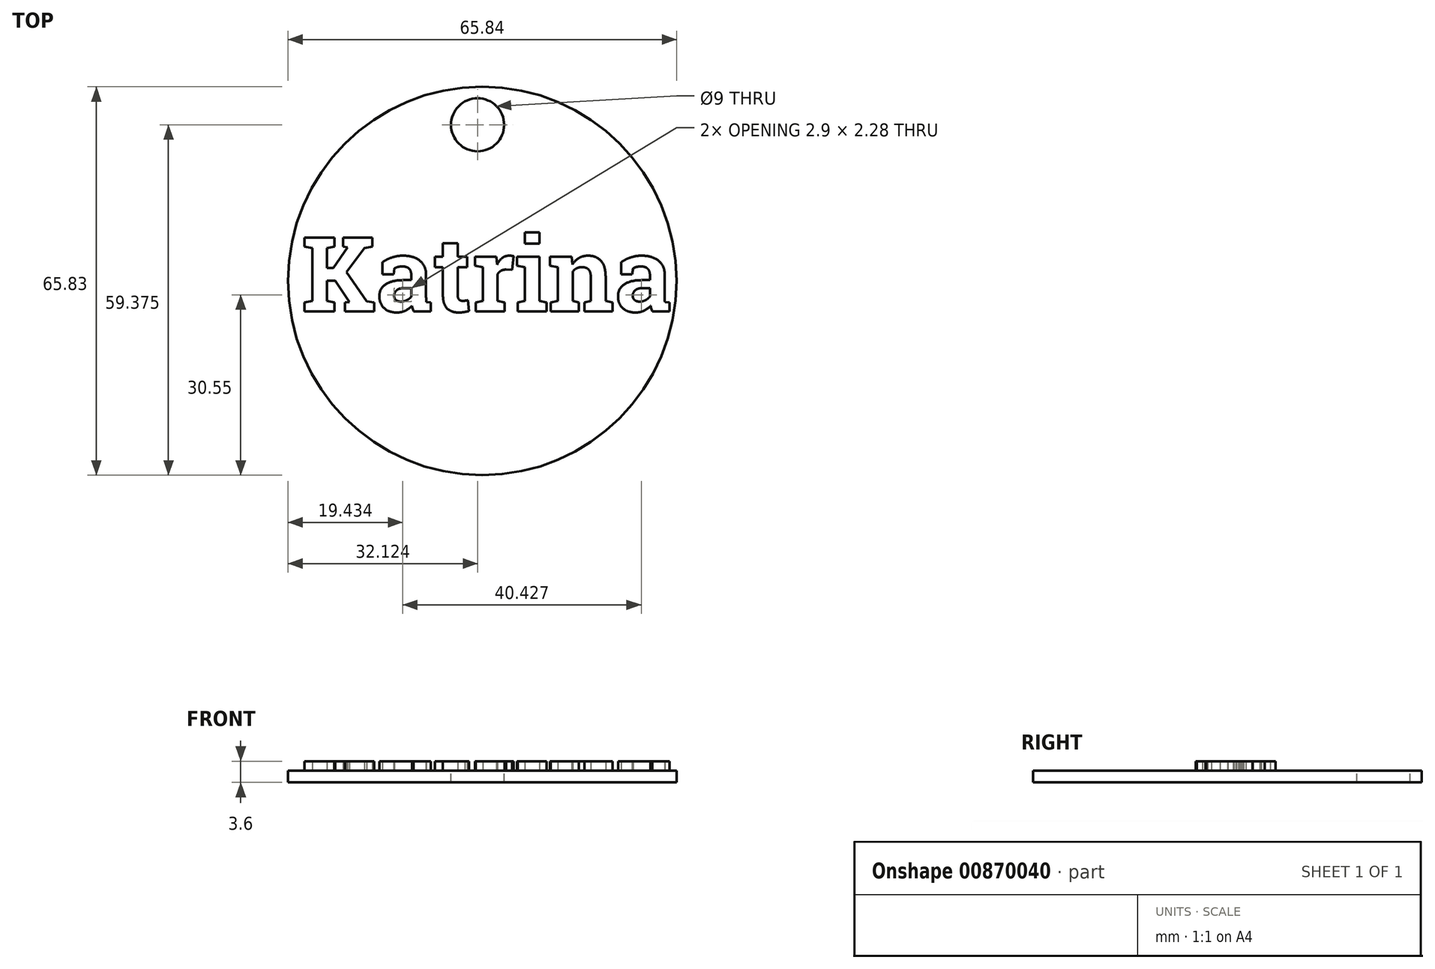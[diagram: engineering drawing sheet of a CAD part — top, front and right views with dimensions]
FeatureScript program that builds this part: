
annotation { "Feature Type Name" : "Feature", "Feature Type Description" : "" }
export const myFeature = defineFeature(function(context is Context, id is Id, definition is map)
    precondition{}
    {
        {
            var Q0;
            Q0=qCreatedBy(makeId("Top.planeOp"),FACE);
            var sketch = newSketch(context, id + "F0", { "sketchPlane" : qUnion([Q0])});
            skText(sketch, "E0", { "text": "Katrina", "fontName": "RobotoSlab-Bold.ttf"});
            const initialGuessF0  = {"E0": [-0.08255, 0.0103, 1, 0, 0.03163]};
            skSetInitialGuess(sketch, initialGuessF0);
            skSolve(sketch);
        }
        {
            var Q0;
            Q0 = qSketchRegion(id + "F0", true);
            extrude(context, id + "F1", {"entities" : qUnion([Q0]), "depth" : 4 * mm, "offsetDistance" : 25.4 * mm});
        }
        {
            var Q0;
            Q0=makeQuery(id+"F1.opExtrude","SWEPT_BODY",BODY,{"disambiguationData":[OSD([sQuery(id+"F0.wireOp",EDGE,"E0.sketch_text.stroke-143"),sQuery(id+"F0.wireOp",EDGE,"E0.sketch_text.stroke-144"),sQuery(id+"F0.wireOp",EDGE,"E0.sketch_text.stroke-145"),sQuery(id+"F0.wireOp",EDGE,"E0.sketch_text.stroke-146"),sQuery(id+"F0.wireOp",EDGE,"E0.sketch_text.stroke-147"),sQuery(id+"F0.wireOp",EDGE,"E0.sketch_text.stroke-148"),sQuery(id+"F0.wireOp",EDGE,"E0.sketch_text.stroke-149"),sQuery(id+"F0.wireOp",EDGE,"E0.sketch_text.stroke-150"),sQuery(id+"F0.wireOp",EDGE,"E0.sketch_text.stroke-151"),sQuery(id+"F0.wireOp",EDGE,"E0.sketch_text.stroke-152"),sQuery(id+"F0.wireOp",EDGE,"E0.sketch_text.stroke-153"),sQuery(id+"F0.wireOp",EDGE,"E0.sketch_text.stroke-154"),sQuery(id+"F0.wireOp",EDGE,"E0.sketch_text.stroke-155"),sQuery(id+"F0.wireOp",EDGE,"E0.sketch_text.stroke-156"),sQuery(id+"F0.wireOp",EDGE,"E0.sketch_text.stroke-157"),sQuery(id+"F0.wireOp",EDGE,"E0.sketch_text.stroke-158"),sQuery(id+"F0.wireOp",EDGE,"E0.sketch_text.stroke-159"),sQuery(id+"F0.wireOp",EDGE,"E0.sketch_text.stroke-160"),sQuery(id+"F0.wireOp",EDGE,"E0.sketch_text.stroke-161"),sQuery(id+"F0.wireOp",EDGE,"E0.sketch_text.stroke-162"),sQuery(id+"F0.wireOp",EDGE,"E0.sketch_text.stroke-163"),sQuery(id+"F0.wireOp",EDGE,"E0.sketch_text.stroke-164"),sQuery(id+"F0.wireOp",EDGE,"E0.sketch_text.stroke-165"),sQuery(id+"F0.wireOp",EDGE,"E0.sketch_text.stroke-166"),sQuery(id+"F0.wireOp",EDGE,"E0.sketch_text.stroke-167"),sQuery(id+"F0.wireOp",EDGE,"E0.sketch_text.stroke-168"),sQuery(id+"F0.wireOp",EDGE,"E0.sketch_text.stroke-169"),sQuery(id+"F0.wireOp",EDGE,"E0.sketch_text.stroke-170"),sQuery(id+"F0.wireOp",EDGE,"E0.sketch_text.stroke-171"),sQuery(id+"F0.wireOp",EDGE,"E0.sketch_text.stroke-172"),sQuery(id+"F0.wireOp",EDGE,"E0.sketch_text.stroke-173"),sQuery(id+"F0.wireOp",EDGE,"E0.sketch_text.stroke-174"),sQuery(id+"F0.wireOp",EDGE,"E0.sketch_text.stroke-175"),sQuery(id+"F0.wireOp",EDGE,"E0.sketch_text.stroke-176"),sQuery(id+"F0.wireOp",EDGE,"E0.sketch_text.stroke-177")])]});
            var Q1;
            Q1=makeQuery(id+"F1.opExtrude","SWEPT_BODY",BODY,{"disambiguationData":[OSD([sQuery(id+"F0.wireOp",EDGE,"E0.sketch_text.stroke-0"),sQuery(id+"F0.wireOp",EDGE,"E0.sketch_text.stroke-1"),sQuery(id+"F0.wireOp",EDGE,"E0.sketch_text.stroke-2"),sQuery(id+"F0.wireOp",EDGE,"E0.sketch_text.stroke-3"),sQuery(id+"F0.wireOp",EDGE,"E0.sketch_text.stroke-4"),sQuery(id+"F0.wireOp",EDGE,"E0.sketch_text.stroke-5"),sQuery(id+"F0.wireOp",EDGE,"E0.sketch_text.stroke-6"),sQuery(id+"F0.wireOp",EDGE,"E0.sketch_text.stroke-7"),sQuery(id+"F0.wireOp",EDGE,"E0.sketch_text.stroke-8"),sQuery(id+"F0.wireOp",EDGE,"E0.sketch_text.stroke-9"),sQuery(id+"F0.wireOp",EDGE,"E0.sketch_text.stroke-10"),sQuery(id+"F0.wireOp",EDGE,"E0.sketch_text.stroke-11"),sQuery(id+"F0.wireOp",EDGE,"E0.sketch_text.stroke-12"),sQuery(id+"F0.wireOp",EDGE,"E0.sketch_text.stroke-13"),sQuery(id+"F0.wireOp",EDGE,"E0.sketch_text.stroke-14"),sQuery(id+"F0.wireOp",EDGE,"E0.sketch_text.stroke-15"),sQuery(id+"F0.wireOp",EDGE,"E0.sketch_text.stroke-16"),sQuery(id+"F0.wireOp",EDGE,"E0.sketch_text.stroke-17"),sQuery(id+"F0.wireOp",EDGE,"E0.sketch_text.stroke-18"),sQuery(id+"F0.wireOp",EDGE,"E0.sketch_text.stroke-19"),sQuery(id+"F0.wireOp",EDGE,"E0.sketch_text.stroke-20"),sQuery(id+"F0.wireOp",EDGE,"E0.sketch_text.stroke-21"),sQuery(id+"F0.wireOp",EDGE,"E0.sketch_text.stroke-22"),sQuery(id+"F0.wireOp",EDGE,"E0.sketch_text.stroke-23"),sQuery(id+"F0.wireOp",EDGE,"E0.sketch_text.stroke-24"),sQuery(id+"F0.wireOp",EDGE,"E0.sketch_text.stroke-25"),sQuery(id+"F0.wireOp",EDGE,"E0.sketch_text.stroke-26"),sQuery(id+"F0.wireOp",EDGE,"E0.sketch_text.stroke-27"),sQuery(id+"F0.wireOp",EDGE,"E0.sketch_text.stroke-28")])]});
            var Q2;
            Q2=makeQuery(id+"F1.opExtrude","SWEPT_BODY",BODY,{"disambiguationData":[OSD([sQuery(id+"F0.wireOp",EDGE,"E0.sketch_text.stroke-29"),sQuery(id+"F0.wireOp",EDGE,"E0.sketch_text.stroke-30"),sQuery(id+"F0.wireOp",EDGE,"E0.sketch_text.stroke-31"),sQuery(id+"F0.wireOp",EDGE,"E0.sketch_text.stroke-32"),sQuery(id+"F0.wireOp",EDGE,"E0.sketch_text.stroke-33"),sQuery(id+"F0.wireOp",EDGE,"E0.sketch_text.stroke-34"),sQuery(id+"F0.wireOp",EDGE,"E0.sketch_text.stroke-35"),sQuery(id+"F0.wireOp",EDGE,"E0.sketch_text.stroke-36"),sQuery(id+"F0.wireOp",EDGE,"E0.sketch_text.stroke-37"),sQuery(id+"F0.wireOp",EDGE,"E0.sketch_text.stroke-38"),sQuery(id+"F0.wireOp",EDGE,"E0.sketch_text.stroke-39"),sQuery(id+"F0.wireOp",EDGE,"E0.sketch_text.stroke-40"),sQuery(id+"F0.wireOp",EDGE,"E0.sketch_text.stroke-41"),sQuery(id+"F0.wireOp",EDGE,"E0.sketch_text.stroke-42"),sQuery(id+"F0.wireOp",EDGE,"E0.sketch_text.stroke-43"),sQuery(id+"F0.wireOp",EDGE,"E0.sketch_text.stroke-44"),sQuery(id+"F0.wireOp",EDGE,"E0.sketch_text.stroke-45"),sQuery(id+"F0.wireOp",EDGE,"E0.sketch_text.stroke-46"),sQuery(id+"F0.wireOp",EDGE,"E0.sketch_text.stroke-47"),sQuery(id+"F0.wireOp",EDGE,"E0.sketch_text.stroke-48"),sQuery(id+"F0.wireOp",EDGE,"E0.sketch_text.stroke-49"),sQuery(id+"F0.wireOp",EDGE,"E0.sketch_text.stroke-50"),sQuery(id+"F0.wireOp",EDGE,"E0.sketch_text.stroke-51"),sQuery(id+"F0.wireOp",EDGE,"E0.sketch_text.stroke-52"),sQuery(id+"F0.wireOp",EDGE,"E0.sketch_text.stroke-53"),sQuery(id+"F0.wireOp",EDGE,"E0.sketch_text.stroke-54"),sQuery(id+"F0.wireOp",EDGE,"E0.sketch_text.stroke-55"),sQuery(id+"F0.wireOp",EDGE,"E0.sketch_text.stroke-56"),sQuery(id+"F0.wireOp",EDGE,"E0.sketch_text.stroke-57"),sQuery(id+"F0.wireOp",EDGE,"E0.sketch_text.stroke-58"),sQuery(id+"F0.wireOp",EDGE,"E0.sketch_text.stroke-59"),sQuery(id+"F0.wireOp",EDGE,"E0.sketch_text.stroke-60"),sQuery(id+"F0.wireOp",EDGE,"E0.sketch_text.stroke-61"),sQuery(id+"F0.wireOp",EDGE,"E0.sketch_text.stroke-62"),sQuery(id+"F0.wireOp",EDGE,"E0.sketch_text.stroke-63")])]});
            var Q3;
            Q3=makeQuery(id+"F1.opExtrude","SWEPT_BODY",BODY,{"disambiguationData":[OSD([sQuery(id+"F0.wireOp",EDGE,"E0.sketch_text.stroke-64"),sQuery(id+"F0.wireOp",EDGE,"E0.sketch_text.stroke-65"),sQuery(id+"F0.wireOp",EDGE,"E0.sketch_text.stroke-66"),sQuery(id+"F0.wireOp",EDGE,"E0.sketch_text.stroke-67"),sQuery(id+"F0.wireOp",EDGE,"E0.sketch_text.stroke-68"),sQuery(id+"F0.wireOp",EDGE,"E0.sketch_text.stroke-69"),sQuery(id+"F0.wireOp",EDGE,"E0.sketch_text.stroke-70"),sQuery(id+"F0.wireOp",EDGE,"E0.sketch_text.stroke-71"),sQuery(id+"F0.wireOp",EDGE,"E0.sketch_text.stroke-72"),sQuery(id+"F0.wireOp",EDGE,"E0.sketch_text.stroke-73"),sQuery(id+"F0.wireOp",EDGE,"E0.sketch_text.stroke-74"),sQuery(id+"F0.wireOp",EDGE,"E0.sketch_text.stroke-75"),sQuery(id+"F0.wireOp",EDGE,"E0.sketch_text.stroke-76"),sQuery(id+"F0.wireOp",EDGE,"E0.sketch_text.stroke-77"),sQuery(id+"F0.wireOp",EDGE,"E0.sketch_text.stroke-78"),sQuery(id+"F0.wireOp",EDGE,"E0.sketch_text.stroke-79"),sQuery(id+"F0.wireOp",EDGE,"E0.sketch_text.stroke-80"),sQuery(id+"F0.wireOp",EDGE,"E0.sketch_text.stroke-81"),sQuery(id+"F0.wireOp",EDGE,"E0.sketch_text.stroke-82"),sQuery(id+"F0.wireOp",EDGE,"E0.sketch_text.stroke-83")])]});
            var Q4;
            Q4=makeQuery(id+"F1.opExtrude","SWEPT_BODY",BODY,{"disambiguationData":[OSD([sQuery(id+"F0.wireOp",EDGE,"E0.sketch_text.stroke-84"),sQuery(id+"F0.wireOp",EDGE,"E0.sketch_text.stroke-85"),sQuery(id+"F0.wireOp",EDGE,"E0.sketch_text.stroke-86"),sQuery(id+"F0.wireOp",EDGE,"E0.sketch_text.stroke-87"),sQuery(id+"F0.wireOp",EDGE,"E0.sketch_text.stroke-88"),sQuery(id+"F0.wireOp",EDGE,"E0.sketch_text.stroke-89"),sQuery(id+"F0.wireOp",EDGE,"E0.sketch_text.stroke-90"),sQuery(id+"F0.wireOp",EDGE,"E0.sketch_text.stroke-91"),sQuery(id+"F0.wireOp",EDGE,"E0.sketch_text.stroke-92"),sQuery(id+"F0.wireOp",EDGE,"E0.sketch_text.stroke-93"),sQuery(id+"F0.wireOp",EDGE,"E0.sketch_text.stroke-94"),sQuery(id+"F0.wireOp",EDGE,"E0.sketch_text.stroke-95"),sQuery(id+"F0.wireOp",EDGE,"E0.sketch_text.stroke-96"),sQuery(id+"F0.wireOp",EDGE,"E0.sketch_text.stroke-97"),sQuery(id+"F0.wireOp",EDGE,"E0.sketch_text.stroke-98"),sQuery(id+"F0.wireOp",EDGE,"E0.sketch_text.stroke-99"),sQuery(id+"F0.wireOp",EDGE,"E0.sketch_text.stroke-100"),sQuery(id+"F0.wireOp",EDGE,"E0.sketch_text.stroke-101"),sQuery(id+"F0.wireOp",EDGE,"E0.sketch_text.stroke-102")])]});
            var Q5;
            Q5=makeQuery(id+"F1.opExtrude","SWEPT_BODY",BODY,{"disambiguationData":[OSD([sQuery(id+"F0.wireOp",EDGE,"E0.sketch_text.stroke-103"),sQuery(id+"F0.wireOp",EDGE,"E0.sketch_text.stroke-104"),sQuery(id+"F0.wireOp",EDGE,"E0.sketch_text.stroke-105"),sQuery(id+"F0.wireOp",EDGE,"E0.sketch_text.stroke-106"),sQuery(id+"F0.wireOp",EDGE,"E0.sketch_text.stroke-107"),sQuery(id+"F0.wireOp",EDGE,"E0.sketch_text.stroke-108"),sQuery(id+"F0.wireOp",EDGE,"E0.sketch_text.stroke-109"),sQuery(id+"F0.wireOp",EDGE,"E0.sketch_text.stroke-110"),sQuery(id+"F0.wireOp",EDGE,"E0.sketch_text.stroke-111"),sQuery(id+"F0.wireOp",EDGE,"E0.sketch_text.stroke-112")])]});
            var Q6;
            Q6=makeQuery(id+"F1.opExtrude","SWEPT_BODY",BODY,{"disambiguationData":[OSD([sQuery(id+"F0.wireOp",EDGE,"E0.sketch_text.stroke-113"),sQuery(id+"F0.wireOp",EDGE,"E0.sketch_text.stroke-114"),sQuery(id+"F0.wireOp",EDGE,"E0.sketch_text.stroke-115"),sQuery(id+"F0.wireOp",EDGE,"E0.sketch_text.stroke-116")])]});
            var Q7;
            Q7=makeQuery(id+"F1.opExtrude","SWEPT_BODY",BODY,{"disambiguationData":[OSD([sQuery(id+"F0.wireOp",EDGE,"E0.sketch_text.stroke-117"),sQuery(id+"F0.wireOp",EDGE,"E0.sketch_text.stroke-118"),sQuery(id+"F0.wireOp",EDGE,"E0.sketch_text.stroke-119"),sQuery(id+"F0.wireOp",EDGE,"E0.sketch_text.stroke-120"),sQuery(id+"F0.wireOp",EDGE,"E0.sketch_text.stroke-121"),sQuery(id+"F0.wireOp",EDGE,"E0.sketch_text.stroke-122"),sQuery(id+"F0.wireOp",EDGE,"E0.sketch_text.stroke-123"),sQuery(id+"F0.wireOp",EDGE,"E0.sketch_text.stroke-124"),sQuery(id+"F0.wireOp",EDGE,"E0.sketch_text.stroke-125"),sQuery(id+"F0.wireOp",EDGE,"E0.sketch_text.stroke-126"),sQuery(id+"F0.wireOp",EDGE,"E0.sketch_text.stroke-127"),sQuery(id+"F0.wireOp",EDGE,"E0.sketch_text.stroke-128"),sQuery(id+"F0.wireOp",EDGE,"E0.sketch_text.stroke-129"),sQuery(id+"F0.wireOp",EDGE,"E0.sketch_text.stroke-130"),sQuery(id+"F0.wireOp",EDGE,"E0.sketch_text.stroke-131"),sQuery(id+"F0.wireOp",EDGE,"E0.sketch_text.stroke-132"),sQuery(id+"F0.wireOp",EDGE,"E0.sketch_text.stroke-133"),sQuery(id+"F0.wireOp",EDGE,"E0.sketch_text.stroke-134"),sQuery(id+"F0.wireOp",EDGE,"E0.sketch_text.stroke-135"),sQuery(id+"F0.wireOp",EDGE,"E0.sketch_text.stroke-136"),sQuery(id+"F0.wireOp",EDGE,"E0.sketch_text.stroke-137"),sQuery(id+"F0.wireOp",EDGE,"E0.sketch_text.stroke-138"),sQuery(id+"F0.wireOp",EDGE,"E0.sketch_text.stroke-139"),sQuery(id+"F0.wireOp",EDGE,"E0.sketch_text.stroke-140"),sQuery(id+"F0.wireOp",EDGE,"E0.sketch_text.stroke-141"),sQuery(id+"F0.wireOp",EDGE,"E0.sketch_text.stroke-142")])]});
            var Q8;
            Q8=qCreatedBy(makeId("Origin.pointOp"),VERTEX);
            transform(context, id + "F2", {"entities" : qUnion([Q0, Q1, Q2, Q3, Q4, Q5, Q6, Q7]), "transformType" : TransformType.SCALE_UNIFORMLY, "scale" : .4, "scalePoint" : qUnion([Q8]), "makeCopy" : false});
        }
        {
            var Q0;
            Q0=qCreatedBy(makeId("Top.planeOp"),FACE);
            var sketch = newSketch(context, id + "F3", { "sketchPlane" : qUnion([Q0])});
            skCircle(sketch, "E1", {"center": v(-2.39, 9.3) * mm, "radius": 32.92 * mm});
            skPoint(sketch, "E2", {"position": v(-3.19, 35.76) * mm});
            skSolve(sketch);
        }
        {
            var Q0;
            Q0=makeQuery(id+"F3.imprint","IMPRINT",FACE,{"disambiguationData":[TD([[makeQuery(id+"F3.imprint","IMPRINT",EDGE,{"derivedFrom":sQuery(id+"F3.wireOp",EDGE,"E1")}),1.0]])]});
            extrude(context, id + "F4", {"entities" : qUnion([Q0]), "oppositeDirection" : true, "depth" : 2 * mm, "offsetDistance" : 25.4 * mm});
        }
        {
            var Q0;
            Q0=sQuery(id+"F3.wireOp",VERTEX,"E2");
            var Q1;
            Q1=makeQuery(id+"F4.opExtrude","SWEPT_BODY",BODY,{"disambiguationData":[OSD([sQuery(id+"F3.wireOp",EDGE,"E1")])]});
            hole(context, id + "F5", {"style" : HoleStyle.SIMPLE, "endStyle" : HoleEndStyle.THROUGH, "holeDiameter" : 9 * mm, "majorDiameter" : 6.35 * mm, "isTappedThrough" : true, "tappedDepth" : 12.7 * mm, "tapClearance" : 3, "locations" : qUnion([Q0]), "scope" : qUnion([Q1])});
        }
    });
